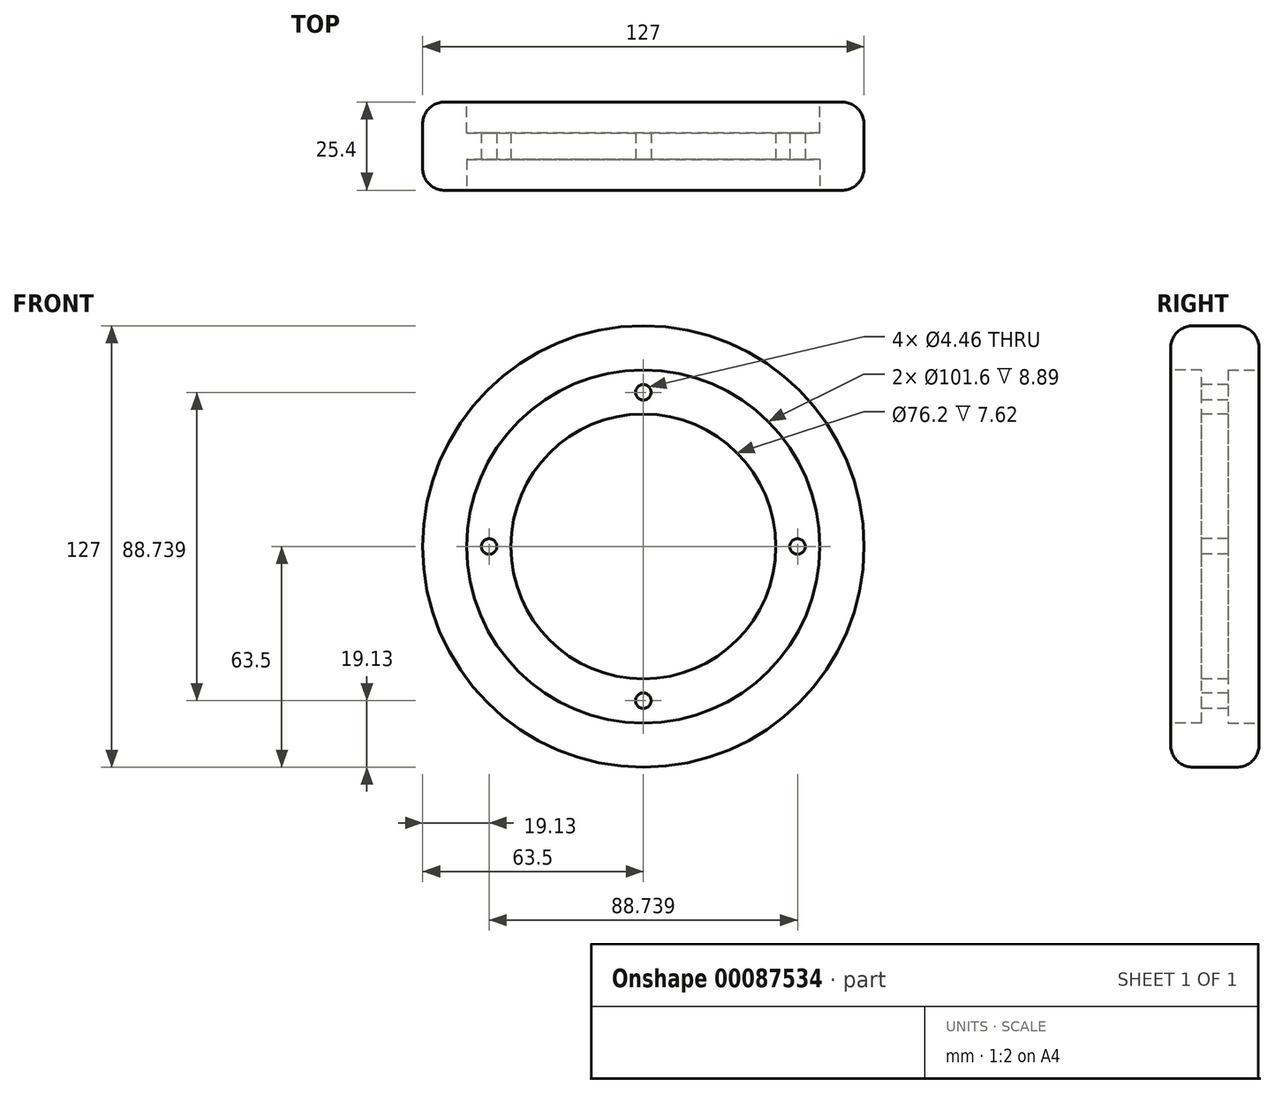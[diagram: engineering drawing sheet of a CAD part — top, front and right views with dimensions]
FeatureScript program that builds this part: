
annotation { "Feature Type Name" : "Feature", "Feature Type Description" : "" }
export const myFeature = defineFeature(function(context is Context, id is Id, definition is map)
    precondition{}
    {
        {
            var Q0;
            Q0=qCreatedBy(makeId("Front.planeOp"),FACE);
            var sketch = newSketch(context, id + "F0", { "sketchPlane" : qUnion([Q0])});
            skCircle(sketch, "E0", {"center": v(0, 0) * mm, "radius": 63.5 * mm});
            skSolve(sketch);
        }
        {
            var Q0;
            Q0=makeQuery(id+"F0.imprint","IMPRINT",FACE,{"disambiguationData":[TD([[makeQuery(id+"F0.imprint","IMPRINT",EDGE,{"derivedFrom":sQuery(id+"F0.wireOp",EDGE,"E0")}),1.0]])]});
            extrude(context, id + "F1", {"entities" : qUnion([Q0]), "endBound" : BoundingType.SYMMETRIC, "depth" : 25.4 * mm});
        }
        {
            var Q0;
            Q0=makeQuery(id+"F1.opExtrude","CAP_EDGE",EDGE,{"disambiguationData":[OSD([sQuery(id+"F0.wireOp",EDGE,"E0")])],"isStart":false});
            var Q1;
            Q1=makeQuery(id+"F1.opExtrude","CAP_EDGE",EDGE,{"disambiguationData":[OSD([sQuery(id+"F0.wireOp",EDGE,"E0")])],"isStart":true});
            fillet(context, id + "F2", {"entities" : qUnion([Q0, Q1]), "radius" : 6.35 * mm, "tangentPropagation" : true, "allowEdgeOverflow" : false});
        }
        {
            var Q0;
            Q0=makeQuery(id+"F1.opExtrude","CAP_FACE",FACE,{"disambiguationData":[OSD([sQuery(id+"F0.wireOp",EDGE,"E0")])],"isStart":false});
            var sketch = newSketch(context, id + "F3", { "sketchPlane" : qUnion([Q0])});
            skCircle(sketch, "E1", {"center": v(0, 0) * mm, "radius": 50.8 * mm});
            skSolve(sketch);
        }
        {
            var Q0;
            Q0=makeQuery(id+"F3.imprint","IMPRINT",FACE,{"disambiguationData":[TD([[makeQuery(id+"F3.imprint","IMPRINT",EDGE,{"derivedFrom":sQuery(id+"F3.wireOp",EDGE,"E1")}),1.0]])]});
            extrude(context, id + "F4", {"entities" : qUnion([Q0]), "operationType" : NewBodyOperationType.REMOVE, "oppositeDirection" : true, "depth" : 8.9 * mm});
        }
        {
            var Q0;
            Q0=makeQuery(id+"F1.opExtrude","CAP_FACE",FACE,{"disambiguationData":[OSD([sQuery(id+"F0.wireOp",EDGE,"E0")])],"isStart":true});
            var sketch = newSketch(context, id + "F5", { "sketchPlane" : qUnion([Q0])});
            skCircle(sketch, "E2", {"center": v(0, 0) * mm, "radius": 50.8 * mm});
            skSolve(sketch);
        }
        {
            var Q0;
            Q0=makeQuery(id+"F5.imprint","IMPRINT",FACE,{"disambiguationData":[TD([[makeQuery(id+"F5.imprint","IMPRINT",EDGE,{"derivedFrom":sQuery(id+"F5.wireOp",EDGE,"E2")}),1.0]])]});
            extrude(context, id + "F6", {"entities" : qUnion([Q0]), "operationType" : NewBodyOperationType.REMOVE, "oppositeDirection" : true, "depth" : 8.9 * mm});
        }
        {
            var Q0;
            Q0=makeQuery(id+"F3.imprint","IMPRINT",FACE,{"disambiguationData":[TD([[makeQuery(id+"F3.imprint","IMPRINT",EDGE,{"derivedFrom":sQuery(id+"F3.wireOp",EDGE,"E1")}),1.0]])]});
            var sketch = newSketch(context, id + "F7", { "sketchPlane" : qUnion([Q0])});
            skCircle(sketch, "E3", {"center": v(0, 0) * mm, "radius": 38.1 * mm});
            skSolve(sketch);
        }
        {
            var Q0;
            Q0=makeQuery(id+"F7.imprint","IMPRINT",FACE,{"disambiguationData":[TD([[makeQuery(id+"F7.imprint","IMPRINT",EDGE,{"derivedFrom":sQuery(id+"F7.wireOp",EDGE,"E3")}),1.0]])]});
            extrude(context, id + "F8", {"entities" : qUnion([Q0]), "operationType" : NewBodyOperationType.REMOVE, "endBound" : BoundingType.THROUGH_ALL, "oppositeDirection" : true, "depth" : 25.4 * mm});
        }
        {
            var Q0;
            Q0=makeQuery(id+"F4.boolean.opBoolean","COPY",FACE,{"derivedFrom":makeQuery(id+"F4.opExtrude","CAP_FACE",FACE,{"disambiguationData":[OSD([sQuery(id+"F3.wireOp",EDGE,"E1")])],"isStart":false})});
            var sketch = newSketch(context, id + "F9", { "sketchPlane" : qUnion([Q0])});
            skCircle(sketch, "E4", {"center": v(0, 44.37) * mm, "radius": 2.23 * mm});
            skCircle(sketch, "E5.1.0", {"center": v(-44.37, 0) * mm, "radius": 2.23 * mm});
            skCircle(sketch, "E5.2.0", {"center": v(0, -44.37) * mm, "radius": 2.23 * mm});
            skCircle(sketch, "E5.3.0", {"center": v(44.37, 0) * mm, "radius": 2.23 * mm});
            skPoint(sketch, "E5.center", {"position": v(0, 0) * mm});
            skSolve(sketch);
        }
        {
            var Q0;
            Q0=makeQuery(id+"F9.imprint","IMPRINT",FACE,{"disambiguationData":[TD([[makeQuery(id+"F9.imprint","IMPRINT",EDGE,{"derivedFrom":sQuery(id+"F9.wireOp",EDGE,"E5.1.0")}),1.0]])]});
            var Q1;
            Q1=makeQuery(id+"F9.imprint","IMPRINT",FACE,{"disambiguationData":[TD([[makeQuery(id+"F9.imprint","IMPRINT",EDGE,{"derivedFrom":sQuery(id+"F9.wireOp",EDGE,"E4")}),1.0]])]});
            var Q2;
            Q2=makeQuery(id+"F9.imprint","IMPRINT",FACE,{"disambiguationData":[TD([[makeQuery(id+"F9.imprint","IMPRINT",EDGE,{"derivedFrom":sQuery(id+"F9.wireOp",EDGE,"E5.3.0")}),1.0]])]});
            var Q3;
            Q3=makeQuery(id+"F9.imprint","IMPRINT",FACE,{"disambiguationData":[TD([[makeQuery(id+"F9.imprint","IMPRINT",EDGE,{"derivedFrom":sQuery(id+"F9.wireOp",EDGE,"E5.2.0")}),1.0]])]});
            var Q4;
            Q4=sQuery(id+"F9.wireOp",EDGE,"E5.1.0");
            var Q5;
            Q5=sQuery(id+"F9.wireOp",EDGE,"E4");
            var Q6;
            Q6=sQuery(id+"F9.wireOp",EDGE,"E5.3.0");
            var Q7;
            Q7=sQuery(id+"F9.wireOp",EDGE,"E5.2.0");
            extrude(context, id + "F10", {"entities" : qUnion([Q0, Q1, Q2, Q3]), "operationType" : NewBodyOperationType.REMOVE, "surfaceEntities" : qUnion([Q4, Q5, Q6, Q7]), "endBound" : BoundingType.THROUGH_ALL, "oppositeDirection" : true, "depth" : 25.4 * mm});
        }
    });
